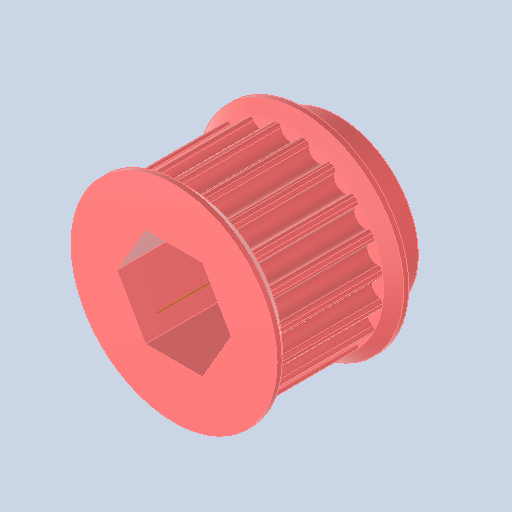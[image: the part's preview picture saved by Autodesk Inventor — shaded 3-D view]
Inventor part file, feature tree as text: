
AUTODESK INVENTOR PART (.ipt)
format: ipt  version: 2022.3 (Build 263350000, 350)  size: 320,000 bytes
history: native  units: in
note: dims shown in document units (in); Inventor stores cm internally (conversion verified against a paired STEP export)
features: extrude x7, sketch x7, mirror x2, chamfer x2, other x1, fillet x1, pattern_circular x1, projected_geometry x1
ambient origin geometry x8: Origin, YZ Plane, XZ Plane, XY Plane, X Axis, Y Axis, Z Axis, Center Point
bodies: Solid1 (feature_tree)
feature tree (22):
  other  "Hex Bore"
  extrude  "HTD Base"  Depth=0.3937in TaperAngle=0.0deg
  extrude  "HTD Flange"  Depth=0.0591in
  mirror  "HTD Flanges"
  chamfer  "HTD Flange Chamfer"  Distance=0.0787in Angle=45.0deg
  extrude  "GT2 Base"  TaperAngle=0.0deg  [1 undecoded]
  extrude  "GT2 Base Tooth"  TaperAngle=0.0deg  [1 undecoded]
  fillet  "GT2 Base Tooth pt. 2"  Radius=0.7219in
  pattern_circular  "GT2 Teeth"  [2 undecoded]
  extrude  "GT2 Flange"  Depth=0.125in
  mirror  "GT2 Flanges"
  chamfer  "GT2 Flange Chamfer"  Distance=0.0075in
  extrude  "Circle Bore"  TaperAngle=0.0deg  [1 undecoded]
  extrude  "Extrusion9"  Depth=0.0118in
  sketch  "Sketch1"  dims[d0=1.2082in d1=0.3937in d2=0.0in]
  sketch  "Sketch4"  dims[d12=0.0394in d13=0.0591in]
  sketch  "Sketch5"  dims[d14=0.0in]
  sketch  "Sketch6"  dims[d15=0.0394in d16=0.0787in d17=45.0deg]
  sketch  "Sketch7"  dims[d18=0.385in d19=0.0in d20=0.0in]
  sketch  "Sketch8"  dims[d21=0.385in d22=0.0in d23=0.0in d24=0.7219in]
  sketch  "Sketch9"  dims[d25=0.3937in d26=0.0in d27=0.0727in d28=0.0075in d29=0.0in d30=0.0in d31=0.0118in d32=7.874in d33=360.0deg d35=0.0394in d36=0.0591in d37=0.0in d38=0.0394in d39=0.0787in d40=45.0deg d41=0.625in d42=0.125in d43=0.0in]
  projected_geometry  "Projected Loop1"
note: 5 required parameter values undecoded (feature->parameter linkage not recoverable at this tier; creation-order binding heuristic only, values carry confidence <= 0.55)
